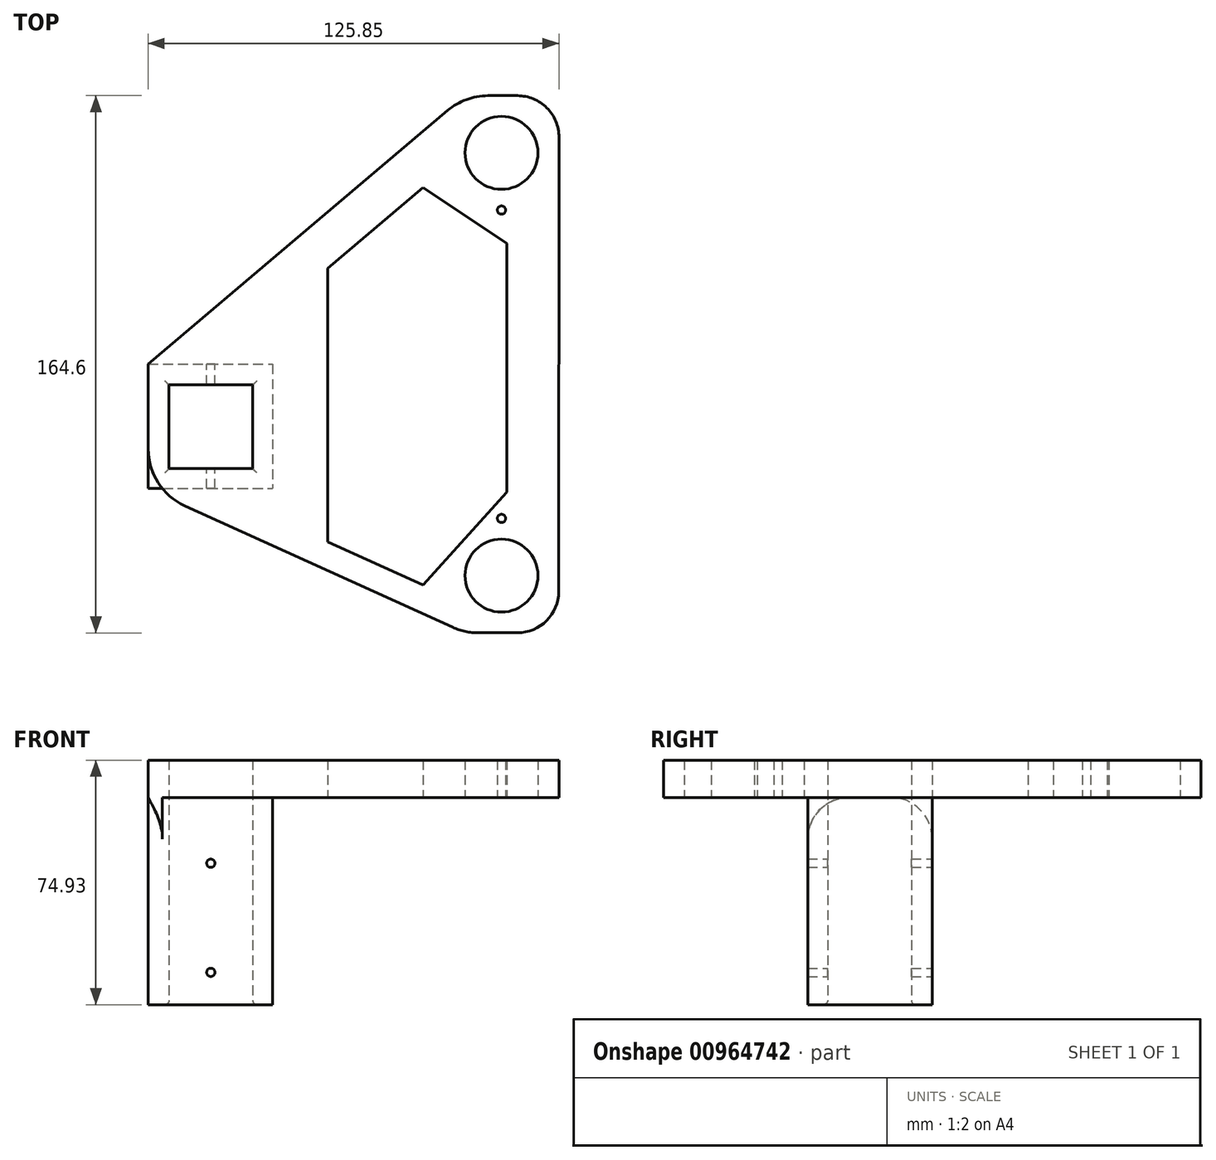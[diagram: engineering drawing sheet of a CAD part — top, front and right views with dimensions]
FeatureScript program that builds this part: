
annotation { "Feature Type Name" : "Feature", "Feature Type Description" : "" }
export const myFeature = defineFeature(function(context is Context, id is Id, definition is map)
    precondition{}
    {
        {
            var Q0;
            Q0=qCreatedBy(makeId("Top.planeOp"),FACE);
            var sketch = newSketch(context, id + "F0", { "sketchPlane" : qUnion([Q0])});
            skLineSegment(sketch, "E0", {"start": v(0, -128.73) * mm, "end": v(0, 148.24) * mm, "construction": true});
            skLineSegment(sketch, "E1", {"start": v(69.65, 0) * mm, "end": v(0, 0) * mm, "construction": true});
            skLineSegment(sketch, "E2", {"start": v(82.28, 64.77) * mm, "end": v(0, 64.77) * mm, "construction": true});
            skLineSegment(sketch, "E3", {"start": v(70.67, -64.77) * mm, "end": v(0, -64.77) * mm, "construction": true});
            skLineSegment(sketch, "E4", {"start": v(76.2, 64.77) * mm, "end": v(76.2, -64.77) * mm, "construction": true});
            skLineSegment(sketch, "E5", {"start": v(-51.25, -6.35) * mm, "end": v(25.13, -6.35) * mm, "construction": true});
            skLineSegment(sketch, "E6.bottom", {"start": v(0, -6.35) * mm, "end": v(-25.65, -6.35) * mm});
            skLineSegment(sketch, "E6.top", {"start": v(0, -32) * mm, "end": v(-25.65, -32) * mm});
            skLineSegment(sketch, "E6.left", {"start": v(0, -6.35) * mm, "end": v(0, -32) * mm});
            skLineSegment(sketch, "E6.right", {"start": v(-25.65, -6.35) * mm, "end": v(-25.65, -32) * mm});
            skCircle(sketch, "E7", {"center": v(76.2, 64.77) * mm, "radius": 11.18 * mm});
            skCircle(sketch, "E8", {"center": v(76.2, -64.77) * mm, "radius": 11.18 * mm});
            skLineSegment(sketch, "E9", {"start": v(-32, 7.55) * mm, "end": v(-32, -38.28) * mm, "construction": true});
            skLineSegment(sketch, "E10", {"start": v(-39.68, -38.35) * mm, "end": v(10.51, -38.35) * mm, "construction": true});
            skLineSegment(sketch, "E11", {"start": v(65.01, -82.3) * mm, "end": v(106.97, -82.3) * mm, "construction": true});
            skLineSegment(sketch, "E12", {"start": v(60.1, 82.3) * mm, "end": v(93.8, 82.3) * mm, "construction": true});
            skLineSegment(sketch, "E13", {"start": v(93.54, 107.03) * mm, "end": v(93.8, -129.71) * mm, "construction": true});
            skLineSegment(sketch, "E14", {"start": v(65.02, 101.34) * mm, "end": v(65.02, -115.62) * mm, "construction": true});
            skLineSegment(sketch, "E15", {"start": v(-32, 0) * mm, "end": v(65.02, 82.3) * mm});
            skLineSegment(sketch, "E16", {"start": v(65.02, 82.3) * mm, "end": v(93.8, 82.3) * mm});
            skLineSegment(sketch, "E17", {"start": v(93.75, -82.3) * mm, "end": v(65.01, -82.3) * mm});
            skLineSegment(sketch, "E18", {"start": v(93.8, 82.3) * mm, "end": v(93.75, -82.3) * mm});
            skLineSegment(sketch, "E19", {"start": v(65.01, -82.3) * mm, "end": v(-32, -38.28) * mm});
            skLineSegment(sketch, "E20", {"start": v(-32, -38.28) * mm, "end": v(-32, 0) * mm});
            skLineSegment(sketch, "E21", {"start": v(60.23, 47.24) * mm, "end": v(85.9, 47.24) * mm, "construction": true});
            skLineSegment(sketch, "E22", {"start": v(68.07, -47.24) * mm, "end": v(79.2, -47.24) * mm, "construction": true});
            skCircle(sketch, "E23", {"center": v(76.2, -47.24) * mm, "radius": 1.27 * mm});
            skCircle(sketch, "E24", {"center": v(76.2, 47.24) * mm, "radius": 1.27 * mm});
            skSolve(sketch);
        }
        {
            var Q0;
            Q0=makeQuery(id+"F0.imprint","IMPRINT",FACE,{"disambiguationData":[TD([[makeQuery(id+"F0.imprint","IMPRINT",EDGE,{"derivedFrom":sQuery(id+"F0.wireOp",EDGE,"E6.bottom")}),-1.0]])]});
            extrude(context, id + "F1", {"entities" : qUnion([Q0]), "depth" : 11.43 * mm, "offsetDistance" : 25.4 * mm});
        }
        {
            var Q0;
            Q0=qCreatedBy(makeId("Top.planeOp"),FACE);
            var sketch = newSketch(context, id + "F2", { "sketchPlane" : qUnion([Q0])});
            skLineSegment(sketch, "E25.bottom", {"start": v(-32.06, 0) * mm, "end": v(6.04, 0) * mm});
            skLineSegment(sketch, "E25.top", {"start": v(-32.06, -38.1) * mm, "end": v(6.04, -38.1) * mm});
            skLineSegment(sketch, "E25.left", {"start": v(-32.06, 0) * mm, "end": v(-32.06, -38.1) * mm});
            skLineSegment(sketch, "E25.right", {"start": v(6.04, 0) * mm, "end": v(6.04, -38.1) * mm});
            skSolve(sketch);
        }
        {
            var Q0;
            Q0 = qSketchRegion(id + "F2", true);
            extrude(context, id + "F3", {"entities" : qUnion([Q0]), "operationType" : NewBodyOperationType.ADD, "oppositeDirection" : true, "depth" : 63.5 * mm, "offsetDistance" : 25.4 * mm});
        }
        {
            var Q0;
            Q0=makeQuery(id+"F3.boolean.opBoolean","SPLIT",FACE,{"disambiguationData":[TD([makeQuery(id+"F1.opExtrude","SWEPT_FACE",FACE,{"disambiguationData":[OSD([sQuery(id+"F0.wireOp",EDGE,"E6.bottom")])]})])],"derivedFrom":makeQuery(id+"F3.opExtrude","CAP_FACE",FACE,{"disambiguationData":[OSD([sQuery(id+"F2.wireOp",EDGE,"E25.bottom"),sQuery(id+"F2.wireOp",EDGE,"E25.top"),sQuery(id+"F2.wireOp",EDGE,"E25.left"),sQuery(id+"F2.wireOp",EDGE,"E25.right")])],"isStart":true})});
            extrude(context, id + "F4", {"entities" : qUnion([Q0]), "operationType" : NewBodyOperationType.REMOVE, "oppositeDirection" : true, "depth" : 76.2 * mm, "offsetDistance" : 25.4 * mm});
        }
        {
            var Q0;
            {var subQ0=sQuery(id+"F2.wireOp",EDGE,"E25.bottom");Q0=makeQuery(id+"F3.boolean.opBoolean","SPLIT",EDGE,{"disambiguationData":[topologyDisambiguationEdgeConnected([makeQuery(id+"F1.opExtrude","CAP_FACE",FACE,{"disambiguationData":[OSD([sQuery(id+"F0.wireOp",EDGE,"E6.bottom"),sQuery(id+"F0.wireOp",EDGE,"E6.top"),sQuery(id+"F0.wireOp",EDGE,"E6.left"),sQuery(id+"F0.wireOp",EDGE,"E6.right"),sQuery(id+"F0.wireOp",EDGE,"E7"),sQuery(id+"F0.wireOp",EDGE,"E8"),sQuery(id+"F0.wireOp",EDGE,"E15"),sQuery(id+"F0.wireOp",EDGE,"E16"),sQuery(id+"F0.wireOp",EDGE,"E18"),sQuery(id+"F0.wireOp",EDGE,"E17"),sQuery(id+"F0.wireOp",EDGE,"E19"),sQuery(id+"F0.wireOp",EDGE,"E20")])],"isStart":true})])],"derivedFrom":makeQuery(id+"F3.opExtrude","CAP_EDGE",EDGE,{"disambiguationData":[OSD([subQ0])],"isStart":true})});}
            var Q1;
            Q1=makeQuery(id+"F3.opExtrude","CAP_EDGE",EDGE,{"disambiguationData":[OSD([sQuery(id+"F2.wireOp",EDGE,"E25.right")])],"isStart":true});
            var Q2;
            {var subQ0=sQuery(id+"F2.wireOp",EDGE,"E25.top");Q2=makeQuery(id+"F3.boolean.opBoolean","SPLIT",EDGE,{"disambiguationData":[topologyDisambiguationEdgeConnected([makeQuery(id+"F1.opExtrude","CAP_FACE",FACE,{"disambiguationData":[OSD([sQuery(id+"F0.wireOp",EDGE,"E6.bottom"),sQuery(id+"F0.wireOp",EDGE,"E6.top"),sQuery(id+"F0.wireOp",EDGE,"E6.left"),sQuery(id+"F0.wireOp",EDGE,"E6.right"),sQuery(id+"F0.wireOp",EDGE,"E7"),sQuery(id+"F0.wireOp",EDGE,"E8"),sQuery(id+"F0.wireOp",EDGE,"E15"),sQuery(id+"F0.wireOp",EDGE,"E16"),sQuery(id+"F0.wireOp",EDGE,"E18"),sQuery(id+"F0.wireOp",EDGE,"E17"),sQuery(id+"F0.wireOp",EDGE,"E19"),sQuery(id+"F0.wireOp",EDGE,"E20")])],"isStart":true})])],"derivedFrom":makeQuery(id+"F3.opExtrude","CAP_EDGE",EDGE,{"disambiguationData":[OSD([subQ0])],"isStart":true})});}
            fillet(context, id + "F5", {"entities" : qUnion([Q0, Q1, Q2]), "radius" : 12.7 * mm, "tangentPropagation" : true, "allowEdgeOverflow" : false});
        }
        {
            var Q0;
            Q0=makeQuery(id+"F1.opExtrude","SWEPT_EDGE",EDGE,{"disambiguationData":[OSD([sQuery(id+"F0.wireOp",EDGE,"E16"),sQuery(id+"F0.wireOp",EDGE,"E18")])]});
            var Q1;
            Q1=makeQuery(id+"F1.opExtrude","SWEPT_EDGE",EDGE,{"disambiguationData":[OSD([sQuery(id+"F0.wireOp",EDGE,"E18"),sQuery(id+"F0.wireOp",EDGE,"E17")])]});
            fillet(context, id + "F6", {"entities" : qUnion([Q0, Q1]), "radius" : 12.7 * mm, "tangentPropagation" : true, "allowEdgeOverflow" : false});
        }
        {
            var Q0;
            Q0=makeQuery(id+"F1.opExtrude","SWEPT_EDGE",EDGE,{"disambiguationData":[OSD([sQuery(id+"F0.wireOp",EDGE,"E17"),sQuery(id+"F0.wireOp",EDGE,"E19")])]});
            var Q1;
            Q1=makeQuery(id+"F1.opExtrude","SWEPT_EDGE",EDGE,{"disambiguationData":[OSD([sQuery(id+"F0.wireOp",EDGE,"E15"),sQuery(id+"F0.wireOp",EDGE,"E16")])]});
            fillet(context, id + "F7", {"entities" : qUnion([Q0, Q1]), "radius" : 19.05 * mm, "tangentPropagation" : true, "allowEdgeOverflow" : false});
        }
        {
            var Q0;
            Q0=makeQuery(id+"F4.boolean.opBoolean","INTERSECT",EDGE,{"derivedFrom":[makeQuery(id+"F3.opExtrude","CAP_FACE",FACE,{"disambiguationData":[OSD([sQuery(id+"F2.wireOp",EDGE,"E25.bottom"),sQuery(id+"F2.wireOp",EDGE,"E25.top"),sQuery(id+"F2.wireOp",EDGE,"E25.left"),sQuery(id+"F2.wireOp",EDGE,"E25.right")])],"isStart":false}),makeQuery(id+"F4.opExtrude","SWEPT_FACE",FACE,{"disambiguationData":[OSD([sQuery(id+"F0.wireOp",EDGE,"E6.right")])]})]});
            var Q1;
            Q1=makeQuery(id+"F4.boolean.opBoolean","INTERSECT",EDGE,{"derivedFrom":[makeQuery(id+"F3.opExtrude","CAP_FACE",FACE,{"disambiguationData":[OSD([sQuery(id+"F2.wireOp",EDGE,"E25.bottom"),sQuery(id+"F2.wireOp",EDGE,"E25.top"),sQuery(id+"F2.wireOp",EDGE,"E25.left"),sQuery(id+"F2.wireOp",EDGE,"E25.right")])],"isStart":false}),makeQuery(id+"F4.opExtrude","SWEPT_FACE",FACE,{"disambiguationData":[OSD([sQuery(id+"F0.wireOp",EDGE,"E6.top")])]})]});
            var Q2;
            Q2=makeQuery(id+"F4.boolean.opBoolean","INTERSECT",EDGE,{"derivedFrom":[makeQuery(id+"F3.opExtrude","CAP_FACE",FACE,{"disambiguationData":[OSD([sQuery(id+"F2.wireOp",EDGE,"E25.bottom"),sQuery(id+"F2.wireOp",EDGE,"E25.top"),sQuery(id+"F2.wireOp",EDGE,"E25.left"),sQuery(id+"F2.wireOp",EDGE,"E25.right")])],"isStart":false}),makeQuery(id+"F4.opExtrude","SWEPT_FACE",FACE,{"disambiguationData":[OSD([sQuery(id+"F0.wireOp",EDGE,"E6.left")])]})]});
            var Q3;
            Q3=makeQuery(id+"F4.boolean.opBoolean","INTERSECT",EDGE,{"derivedFrom":[makeQuery(id+"F3.opExtrude","CAP_FACE",FACE,{"disambiguationData":[OSD([sQuery(id+"F2.wireOp",EDGE,"E25.bottom"),sQuery(id+"F2.wireOp",EDGE,"E25.top"),sQuery(id+"F2.wireOp",EDGE,"E25.left"),sQuery(id+"F2.wireOp",EDGE,"E25.right")])],"isStart":false}),makeQuery(id+"F4.opExtrude","SWEPT_FACE",FACE,{"disambiguationData":[OSD([sQuery(id+"F0.wireOp",EDGE,"E6.bottom")])]})]});
            fillet(context, id + "F8", {"entities" : qUnion([Q0, Q1, Q2, Q3]), "radius" : 1.27 * mm, "tangentPropagation" : true, "allowEdgeOverflow" : false});
        }
        {
            var Q0;
            Q0=qCreatedBy(makeId("Front.planeOp"),FACE);
            var sketch = newSketch(context, id + "F9", { "sketchPlane" : qUnion([Q0])});
            skLineSegment(sketch, "E26", {"start": v(-12.84, -65.94) * mm, "end": v(-12.84, -8.76) * mm, "construction": true});
            skCircle(sketch, "E27", {"center": v(-12.84, -20.17) * mm, "radius": 1.27 * mm});
            skCircle(sketch, "E28", {"center": v(-12.84, -53.59) * mm, "radius": 1.27 * mm});
            skSolve(sketch);
        }
        {
            var Q0;
            Q0 = qSketchRegion(id + "F9", true);
            extrude(context, id + "F10", {"entities" : qUnion([Q0]), "operationType" : NewBodyOperationType.REMOVE, "depth" : 127 * mm, "offsetDistance" : 25.4 * mm});
        }
        {
            var Q0;
            Q0=makeQuery(id+"F1.opExtrude","CAP_FACE",FACE,{"disambiguationData":[OSD([sQuery(id+"F0.wireOp",EDGE,"E6.bottom"),sQuery(id+"F0.wireOp",EDGE,"E6.top"),sQuery(id+"F0.wireOp",EDGE,"E6.left"),sQuery(id+"F0.wireOp",EDGE,"E6.right"),sQuery(id+"F0.wireOp",EDGE,"E7"),sQuery(id+"F0.wireOp",EDGE,"E8"),sQuery(id+"F0.wireOp",EDGE,"E15"),sQuery(id+"F0.wireOp",EDGE,"E16"),sQuery(id+"F0.wireOp",EDGE,"E18"),sQuery(id+"F0.wireOp",EDGE,"E17"),sQuery(id+"F0.wireOp",EDGE,"E19"),sQuery(id+"F0.wireOp",EDGE,"E20"),sQuery(id+"F0.wireOp",EDGE,"E23"),sQuery(id+"F0.wireOp",EDGE,"E24")])],"isStart":true});
            var sketch = newSketch(context, id + "F11", { "sketchPlane" : qUnion([Q0])});
            skLineSegment(sketch, "E29", {"start": v(22.93, 54.38) * mm, "end": v(52.2, 67.67) * mm});
            skLineSegment(sketch, "E30", {"start": v(52.2, 67.67) * mm, "end": v(77.86, 39.2) * mm});
            skLineSegment(sketch, "E31", {"start": v(77.86, 39.2) * mm, "end": v(77.86, -37.06) * mm});
            skLineSegment(sketch, "E32", {"start": v(77.86, -37.06) * mm, "end": v(52.2, -54.2) * mm});
            skLineSegment(sketch, "E33", {"start": v(52.2, -54.2) * mm, "end": v(22.93, -29.37) * mm});
            skLineSegment(sketch, "E34", {"start": v(22.93, -29.37) * mm, "end": v(22.93, 54.38) * mm});
            skSolve(sketch);
        }
        {
            var Q0;
            Q0 = qSketchRegion(id + "F11", true);
            extrude(context, id + "F12", {"entities" : qUnion([Q0]), "operationType" : NewBodyOperationType.REMOVE, "endBound" : BoundingType.THROUGH_ALL, "oppositeDirection" : true, "depth" : 25.4 * mm, "offsetDistance" : 25.4 * mm});
        }
    });
